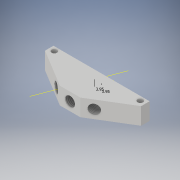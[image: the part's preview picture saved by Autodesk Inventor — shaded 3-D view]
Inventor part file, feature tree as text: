
AUTODESK INVENTOR PART (.ipt)
format: ipt  version: 2018 (Build 220112000, 112)  size: 172,544 bytes
history: native  units: in
note: dims shown in document units (in); Inventor stores cm internally (conversion verified against a paired STEP export)
features: sketch x12, extrude x6, other x6, thread x3, hole x2
ambient origin geometry x8: Origin, YZ Plane, XZ Plane, XY Plane, X Axis, Y Axis, Z Axis, Center Point
bodies: Solid1 (feature_tree)
feature tree (29):
  extrude  "Extrusion1"  Depth=1.1122in
  extrude  "Extrusion2"  Depth=0.7283in
  extrude  "Extrusion3"  Depth=0.3937in
  thread  "Thread1"  [1 undecoded]
  extrude  "Extrusion4"  Depth=0.1181in
  extrude  "Extrusion5"  Depth=0.3937in
  thread  "Thread2"  [1 undecoded]
  thread  "Thread3"  [1 undecoded]
  extrude  "Extrusion6"  Depth=0.1969in
  sketch  "Sketch14"  dims[d17=0.2756in d18=0.0in d19=0.3937in d20=0.0in]
  other  "Work Point2"
  sketch  "Sketch19"  dims[d21=0.2268in d22=0.2362in]
  other  "Work Point5"
  sketch  "3D Sketch5"
  other  "Work Axis3"
  hole  "Hole1"  [1 undecoded]
  sketch  "Sketch20"  dims[d23=0.1969in]
  other  "Work Point6"
  sketch  "Sketch21"  dims[d24=0.2756in d25=0.0in d26=0.2268in d27=0.1969in d28=0.2362in d29=0.2756in d30=0.0in d31=0.3937in d32=0.0in d33=0.3937in d34=0.0in d35=0.0591in d36=0.4724in d37=0.0in d50=0.1555in d60=0.3937in d61=0.3937in d53=0.07in d54=0.2362in d55=0.1575in d56=0.0787in d57=90.0deg d58=0.7973in d59=0.7559in d62=0.1555in d63=0.3937in d64=0.3937in d65=0.0591in d66=0.2362in d67=0.1575in d68=0.0787in d69=90.0deg d70=0.7973in d71=0.7559in d44=0.0394in d45=0.0394in d47=0.0394in d48=0.0394in d51=0.0394in d52=0.0394in]
  other  "Work Point7"
  sketch  "3D Sketch6"
  other  "Work Axis4"
  hole  "Hole2"  [1 undecoded]
  sketch  "Sketch1"  dims[d0=1.1122in d1=1.1122in]
  sketch  "Sketch2"  dims[d2=0.7283in d3=0.2362in]
  sketch  "Sketch3"  dims[d4=0.2362in d5=0.1969in d6=0.3937in d7=0.0in]
  sketch  "Sketch4"  dims[d8=0.126in d9=0.1181in]
  sketch  "Sketch5"  dims[d10=0.0984in d11=0.126in d12=0.1181in d13=0.3937in d14=0.0in]
  sketch  "Sketch6"  dims[d15=0.2268in d16=0.1969in]
note: 5 required parameter values undecoded (feature->parameter linkage not recoverable at this tier; creation-order binding heuristic only, values carry confidence <= 0.55)
